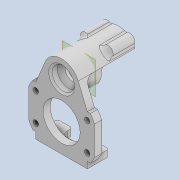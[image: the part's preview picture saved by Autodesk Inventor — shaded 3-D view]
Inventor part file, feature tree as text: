
AUTODESK INVENTOR PART (.ipt)
format: ipt  version: 2020 (Build 240168000, 168)  size: 500,224 bytes
history: native  units: mm
features: extrude x15, sketch x15, reference x11, projected_geometry x10, other x6, fillet x5, chamfer x4, plane x3, thicken_offset x2
ambient origin geometry x8: Origin, YZ Plane, XZ Plane, XY Plane, X Axis, Y Axis, Z Axis, Center Point
bodies: Solid1 (feature_tree)
feature tree (71):
  extrude  "Extrusion1"  Depth=12.0mm
  extrude  "Extrusion2"  Depth=12.0mm
  extrude  "Extrusion3"  Depth=2.2mm
  plane  "Work Plane1"
  extrude  "Extrusion4"  Depth=10.0mm
  chamfer  "Chamfer1"  Distance=2.0mm
  extrude  "Extrusion5"  Depth=4.8mm TaperAngle=0.0deg
  extrude  "Extrusion6"  Depth=4.8mm TaperAngle=0.0deg
  extrude  "Extrusion7"  Depth=1.0mm
  plane  "Work Plane2"
  sketch  "Sketch10"  dims[d18=2.8mm d19=0.0mm d20=1.0mm d21=2.0mm d22=45.0deg]
  plane  "Work Plane4"
  extrude  "Extrusion10"  Depth=1.0mm TaperAngle=45.0deg
  extrude  "Extrusion11"  Depth=14.3mm
  fillet  "Fillet1"  Radius=1.8mm
  fillet  "Fillet2"  Radius=2.8mm
  extrude  "Extrusion13"  Depth=4.0mm TaperAngle=0.0deg
  extrude  "Extrusion14"  Depth=4.0mm
  fillet  "Fillet5"  Radius=8.37758mm
  chamfer  "Chamfer2"  Distance=4.0mm
  thicken_offset  "Thicken1"
  thicken_offset  "Thicken2"
  chamfer  "Chamfer5"  Distance=2.0mm
  extrude  "Extrusion15"  Depth=4.5mm
  extrude  "Extrusion18"  Depth=4.5mm
  fillet  "Fillet8"  Radius=4.0mm
  fillet  "Fillet9"  Radius=6.0mm
  extrude  "Extrusion19"  Depth=3.0mm
  extrude  "Extrusion20"  Depth=4.5mm TaperAngle=0.0deg
  chamfer  "Chamfer6"  Distance=1.5mm
  sketch  "Sketch1"  dims[d0=4.0mm d1=12.0mm]
  reference  "Reference1"
  reference  "Reference2"
  sketch  "Sketch2"  dims[d2=4.0mm d3=12.0mm]
  projected_geometry  "Projected Loop1"
  sketch  "Sketch3"  dims[d4=16.0mm d5=2.2mm]
  projected_geometry  "Projected Loop2"
  sketch  "Sketch4"  dims[d6=6.0mm d7=10.0mm d8=2.0mm d9=0.0mm]
  sketch  "Sketch5"  dims[d10=8.5mm d11=4.8mm d12=0.0mm]
  projected_geometry  "Projected Loop3"
  sketch  "Sketch6"  dims[d13=3.9mm d14=4.8mm d15=0.0mm]
  projected_geometry  "Projected Loop4"
  sketch  "Sketch7"  dims[d16=-2.0mm d17=1.0mm]
  reference  "Reference3"
  reference  "Reference4"
  reference  "Reference7"
  sketch  "Sketch11"  dims[d23=10.3mm d24=14.3mm d25=1.8mm d26=2.8mm d27=0.0mm]
  reference  "Reference8"
  sketch  "Sketch13"  dims[d28=4.0mm d29=0.0mm d30=4.0mm d31=0.0mm]
  projected_geometry  "Projected Loop9"
  sketch  "Sketch14"  dims[d42=4.0mm d43=0.0mm d44=4.0mm d45=8.37758mm]
  projected_geometry  "Projected Loop10"
  reference  "Reference10"
  sketch  "Sketch15"  dims[d46=1.2mm]
  projected_geometry  "Projected Loop11"
  projected_geometry  "Projected Loop12"
  sketch  "Sketch18"  dims[d47=4.0mm]
  reference  "Reference13"
  reference  "Reference14"
  reference  "Reference15"
  reference  "Reference16"
  sketch  "Sketch19"  dims[d48=8.37758mm]
  projected_geometry  "Projected Loop13"
  sketch  "Sketch20"  dims[d49=1.2mm d50=4.0mm d51=0.0mm d52=2.0mm d53=1.5mm d59=20.0mm d60=4.0mm d61=0.0mm d62=6.0mm d63=3.0mm d64=4.0mm d65=0.0mm d66=1.5mm d67=0.5mm d68=2.0mm d69=45.0deg d73=0.1mm d74=0.15mm d75=0.1mm d76=0.15mm d80=0.5mm d81=2.0mm d82=45.0deg d83=6.0mm d84=0.0mm d93=2.8mm d94=2.8mm d95=6.0mm d96=0.0mm d97=2.0mm d98=1.0mm d99=1.4mm d100=1.4mm d101=4.5mm d102=0.0mm d103=0.25mm d104=7.0mm d105=0.0mm d106=0.25mm d107=2.0mm d108=45.0deg]
  projected_geometry  "Projected Loop14"
  parser-record x1  (decoder bookkeeping rows leaked as tree rows — omitted from the tree; the rows remain in map.json)
  other  "tip_ass_t1.iam"
  other  "motor_1608:1"
  other  "motor_1608_inner:1"
  other  "motor_1608_outer:1"
  other  "pin_conn_2:1"
note: 1 file-system path scrubbed to <path> (originals preserved in map.json)
